# Revit family: KFL3
name_source: partatom
category: Lighting Fixtures
units: mm (PartAtom-declared; Revit-internal decimal feet)

## family parameters
Cut with Voids When Loaded = No
Host = Face
Light Source = Yes
OmniClass Number = 23.80.70.14.14
OmniClass Title = Exterior Floodlights
Part Type = Normal
Room Calculation Point = No
Round Connector Dimension = Use Diameter
Shared = Yes

## types (1)
- KFL3-33L
    Apparent Load = 75 VA
    Assembly Code = D5020200
    Certifications = UL 1598, IP66 certified, UL8750(LED Lighting)
    Color Filter = 16777215
    Connector Description = Lighting Connector
    Default Elevation = 48 "
    Description = The Kim Architectural Flood is a striking timeless form that seamlessly blends high performance optics, controls, scalability and architectural mounting options which cover a wide variety of applications and enhance their environment. RGBW floods adds drama and theatricality to the site.
    Dimming Lamp Color Temperature Shift = <None>
    Features = Color Temperatures: Red, Green, Blue, White
(5700K) and Red, Green, Blue, Warm White
(2700K).
• Yoke and Threaded Knuckle mounting options.
• IP66 sealed optical and driver chamber.
• 7 beam distributions for applications
including Narrow Spot 6°x6°, Spot 8°x8°,
Narrow 24°x24°, Medium 39°x39°, Medium
Flood 45°x51°, Horizontal 39°x9°, and
Vertical 9°x39°.
    Housing Material = Paint - Carbon Black
    LED_Config = KL : 33L
    Lamp = LED
    Length = 26.38 "
    Load Classification = Lighting
    Manufacturer = Kim Lighting
    Model = KFL3RGBW
    Photometric Note = For more ies file please find the above Photometric Web Link
    Photometric Web File = KFL3-33L-75-RGBW-SP.ies
    Power Factor = 1
    Reflector Finish = White Glass
    Tilt Angle = 0.00°
    URL = https://www.currentlighting.com
    Voltage = 120 V
    Warranty = 5 years Warranty
    Wattage Comments = 75W
    Watts = 75 W
    Width = 11.63 "
    Width 1 = 5 "

## geometry (parser evidence)
native form markers: Sweep x4
no freeform markers — native parametric forms only
